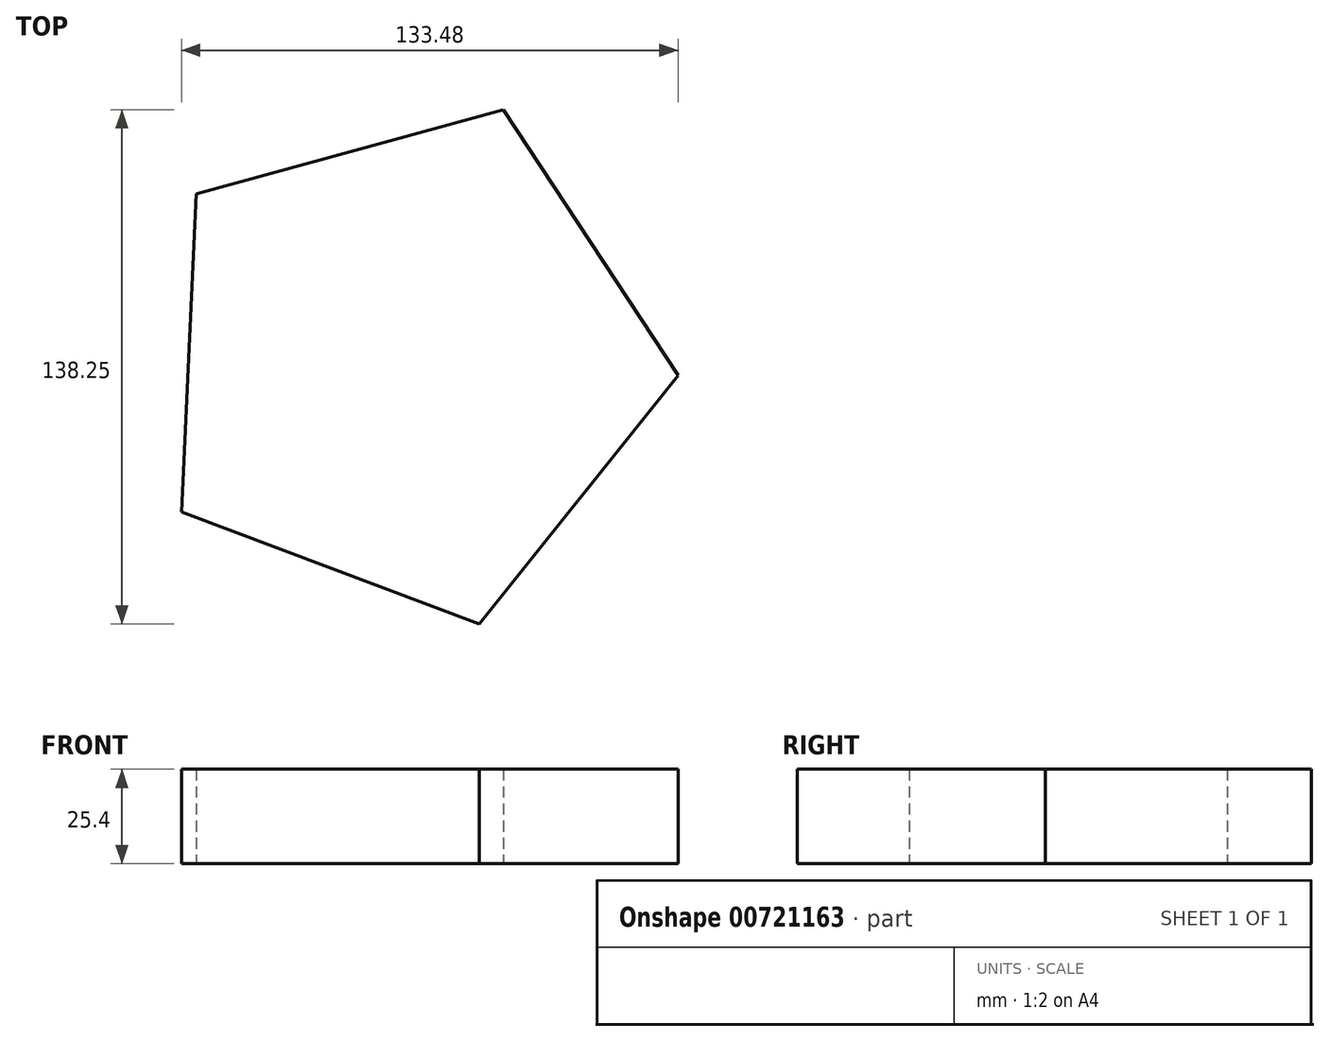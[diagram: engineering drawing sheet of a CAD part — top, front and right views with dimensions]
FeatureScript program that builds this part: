
annotation { "Feature Type Name" : "Feature", "Feature Type Description" : "" }
export const myFeature = defineFeature(function(context is Context, id is Id, definition is map)
    precondition{}
    {
        {
            var Q0;
            Q0=qCreatedBy(makeId("Top.planeOp"),FACE);
            var sketch = newSketch(context, id + "F0", { "sketchPlane" : qUnion([Q0])});
            skCircle(sketch, "E0.cCircle", {"center": v(-62.5, 20.73) * mm, "radius": 58.86 * mm, "construction": true});
            skLineSegment(sketch, "E0.0", {"start": v(10.19, 17.34) * mm, "end": v(-43.26, -49.44) * mm});
            skLineSegment(sketch, "E0.1", {"start": v(-43.26, -49.44) * mm, "end": v(-123.29, -19.24) * mm});
            skLineSegment(sketch, "E0.2", {"start": v(-123.29, -19.24) * mm, "end": v(-119.3, 66.2) * mm});
            skLineSegment(sketch, "E0.3", {"start": v(-119.3, 66.2) * mm, "end": v(-36.8, 88.8) * mm});
            skLineSegment(sketch, "E0.4", {"start": v(-36.8, 88.8) * mm, "end": v(10.19, 17.34) * mm});
            skPoint(sketch, "E0.0.midPoint", {"position": v(-16.54, -16.05) * mm});
            skSolve(sketch);
        }
        {
            var Q0;
            Q0=makeQuery(id+"F0.imprint","IMPRINT",FACE,{"disambiguationData":[TD([[makeQuery(id+"F0.imprint","IMPRINT",EDGE,{"derivedFrom":sQuery(id+"F0.wireOp",EDGE,"E0.0")}),-1.0]])]});
            extrude(context, id + "F1", {"entities" : qUnion([Q0]), "depth" : 25.4 * mm, "offsetDistance" : 25.4 * mm});
        }
    });
